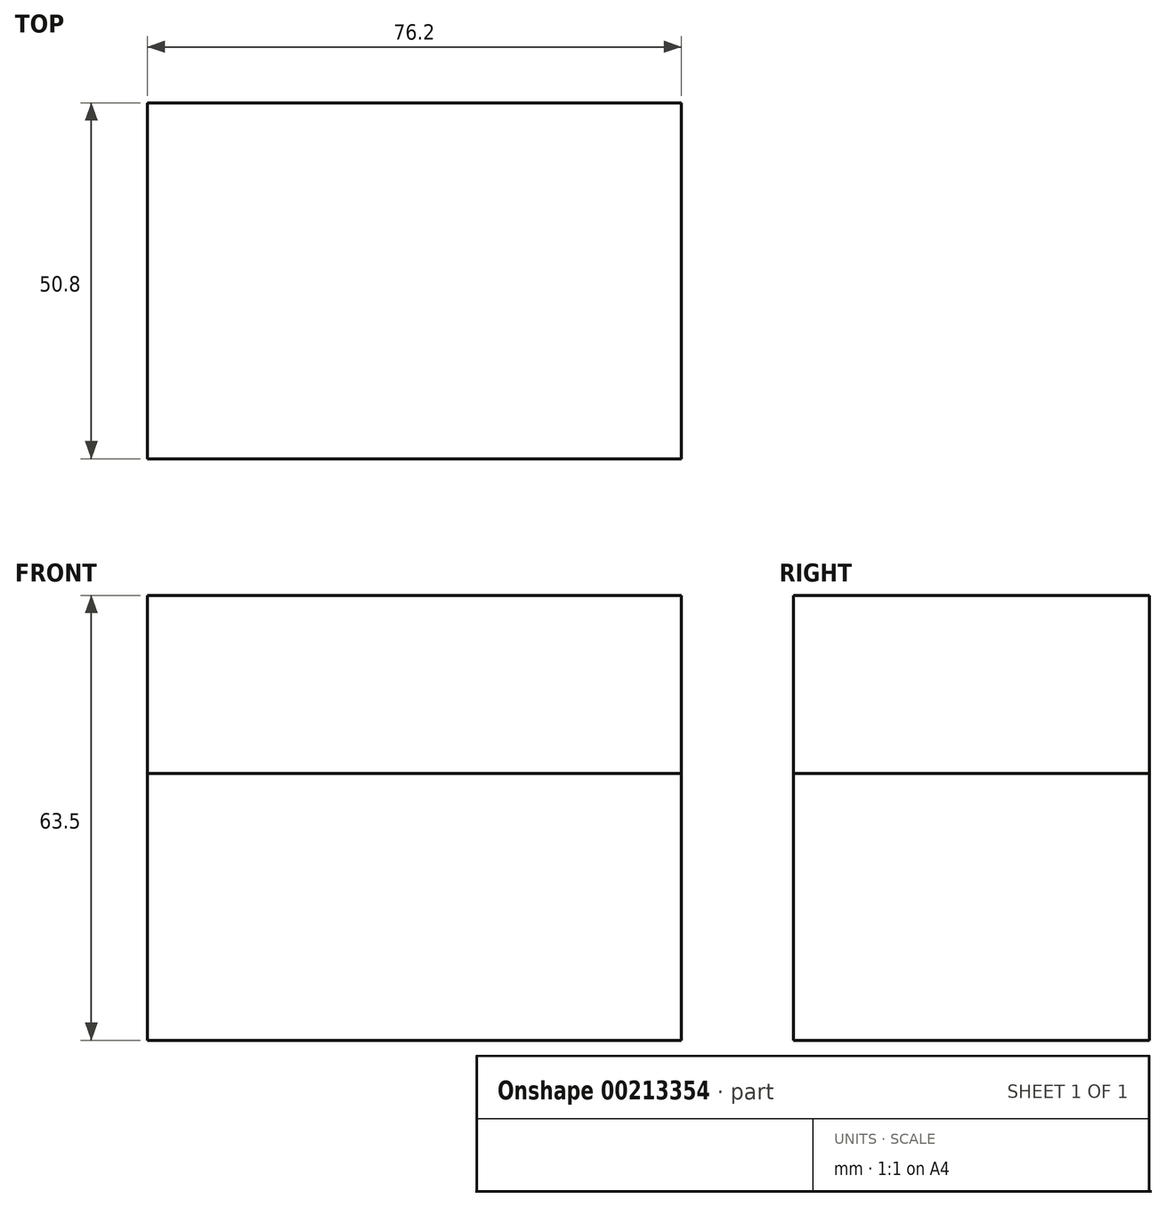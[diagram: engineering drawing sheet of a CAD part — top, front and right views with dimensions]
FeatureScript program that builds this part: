
annotation { "Feature Type Name" : "Feature", "Feature Type Description" : "" }
export const myFeature = defineFeature(function(context is Context, id is Id, definition is map)
    precondition{}
    {
        {
            var Q0;
            Q0=qCreatedBy(makeId("Top.planeOp"),FACE);
            var sketch = newSketch(context, id + "F0", { "sketchPlane" : qUnion([Q0])});
            skLineSegment(sketch, "E0.bottom", {"start": v(38.1, -25.4) * mm, "end": v(-38.1, -25.4) * mm});
            skLineSegment(sketch, "E0.top", {"start": v(38.1, 25.4) * mm, "end": v(-38.1, 25.4) * mm});
            skLineSegment(sketch, "E0.left", {"start": v(38.1, -25.4) * mm, "end": v(38.1, 25.4) * mm});
            skLineSegment(sketch, "E0.right", {"start": v(-38.1, -25.4) * mm, "end": v(-38.1, 25.4) * mm});
            skPoint(sketch, "E0.middle", {"position": v(0, 0) * mm});
            skLineSegment(sketch, "E1", {"start": v(-38.1, 0) * mm, "end": v(38.1, 0) * mm});
            skSolve(sketch);
        }
        {
            var Q0;
            {var subQ0=sQuery(id+"F0.wireOp",EDGE,"E0.top");Q0=makeQuery(id+"F0.imprint","IMPRINT",FACE,{"disambiguationData":[TD([[makeQuery(id+"F0.imprint","IMPRINT",EDGE,{"derivedFrom":subQ0}),1.0]])]});}
            var Q1;
            {var subQ0=sQuery(id+"F0.wireOp",EDGE,"E0.bottom");Q1=makeQuery(id+"F0.imprint","IMPRINT",FACE,{"disambiguationData":[TD([[makeQuery(id+"F0.imprint","IMPRINT",EDGE,{"derivedFrom":subQ0}),-1.0]])]});}
            extrude(context, id + "F1", {"entities" : qUnion([Q0, Q1]), "endBound" : BoundingType.SYMMETRIC, "depth" : 25.4 * mm});
        }
        {
            var Q0;
            Q0=makeQuery(id+"F1.opExtrude","CAP_FACE",FACE,{"disambiguationData":[OSD([sQuery(id+"F0.wireOp",EDGE,"E0.top"),sQuery(id+"F0.wireOp",EDGE,"E0.left"),sQuery(id+"F0.wireOp",EDGE,"E0.right"),sQuery(id+"F0.wireOp",EDGE,"E1")])],"isStart":true});
            extrude(context, id + "F2", {"entities" : qUnion([Q0]), "depth" : 38.1 * mm});
        }
    });
